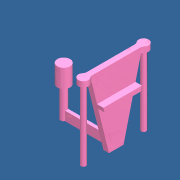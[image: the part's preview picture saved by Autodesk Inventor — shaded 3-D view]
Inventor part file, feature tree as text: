
AUTODESK INVENTOR PART (.ipt)
format: ipt  version: 2020 (Build 240168000, 168)  size: 219,648 bytes
history: native  units: mm
features: extrude x9, sketch x9, mirror x1, chamfer x1, fillet x1, projected_geometry x1
ambient origin geometry x8: Origin, YZ Plane, XZ Plane, XY Plane, X Axis, Y Axis, Z Axis, Center Point
bodies: Solid1 (feature_tree)
feature tree (22):
  extrude  "Extrusion1"  Depth=33.0mm TaperAngle=0.0deg
  extrude  "Extrusion2"  Depth=20.0mm TaperAngle=0.0deg
  extrude  "Extrusion3"  Depth=10.0mm
  extrude  "Extrusion4"  Depth=8.0mm
  extrude  "Extrusion5"  Depth=77.0mm
  extrude  "Extrusion6"  Depth=6.0mm TaperAngle=0.0deg
  extrude  "Extrusion7"  Depth=33.0mm
  mirror  "Mirror1"
  extrude  "Extrusion8"  Depth=6.0mm TaperAngle=0.0deg
  extrude  "Extrusion9"  Depth=2.0mm TaperAngle=0.0deg
  chamfer  "Chamfer1"  Distance=30.0mm
  fillet  "Fillet1"  Radius=7.0mm
  sketch  "Sketch1"  dims[d0=7.0mm d1=33.0mm d2=0.0mm]
  sketch  "Sketch2"  dims[d3=14.0mm d4=20.0mm d5=0.0mm]
  sketch  "Sketch3"  dims[d6=57.5mm d7=10.0mm]
  sketch  "Sketch4"  dims[d8=3.5mm d9=0.0mm d10=8.0mm]
  sketch  "Sketch5"  dims[d11=27.0mm d12=77.0mm]
  projected_geometry  "Projected Loop1"
  sketch  "Sketch6"  dims[d13=6.0mm d14=0.0mm d15=6.0mm d16=0.0mm]
  sketch  "Sketch7"  dims[d17=11.0mm d18=33.0mm]
  sketch  "Sketch8"  dims[d19=3.0mm d20=6.0mm d21=0.0mm]
  sketch  "Sketch10"  dims[d22=5.5mm d23=77.0mm d24=0.0mm d27=30.0mm d28=7.0mm d29=0.0mm d30=5.0mm d31=50.0mm d32=5.0mm d33=20.0mm d34=0.0mm d35=15.0mm d36=2.0mm d37=45.0deg d38=2.0mm]
